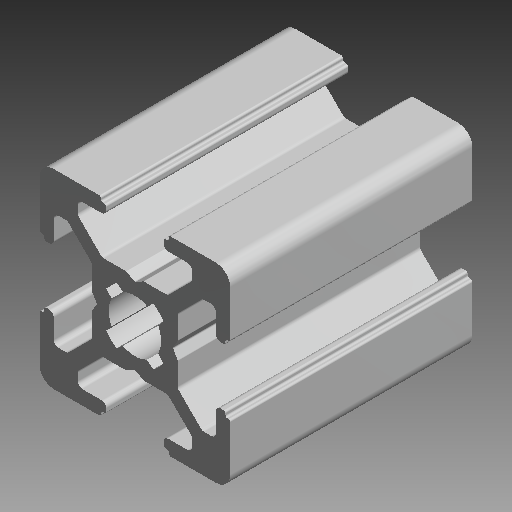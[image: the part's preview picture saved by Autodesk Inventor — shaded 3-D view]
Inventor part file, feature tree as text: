
AUTODESK INVENTOR PART (.ipt)
format: ipt  version: 2019 (Build 230136000, 136)  size: 389,632 bytes
history: native  units: mm (DEFAULTED — no unit token found)
features: other x5, sketch x1
ambient origin geometry x8: Origin, YZ Plane, XZ Plane, XY Plane, X Axis, Y Axis, Z Axis, Center Point
bodies: Solid1 (feature_tree)
feature tree (6):
  other  "Bosch 20x20 - 1.5 Part.Shoot.ipt"
  other  "Blocks"
  other  "20x20"
  other  "Solid1::Bosch 20x20 - 1.5 Part.Shoot.ipt"
  other  "TaggingFeature1"
  sketch  "Sketch1"  dims[d0=10.0mm]
